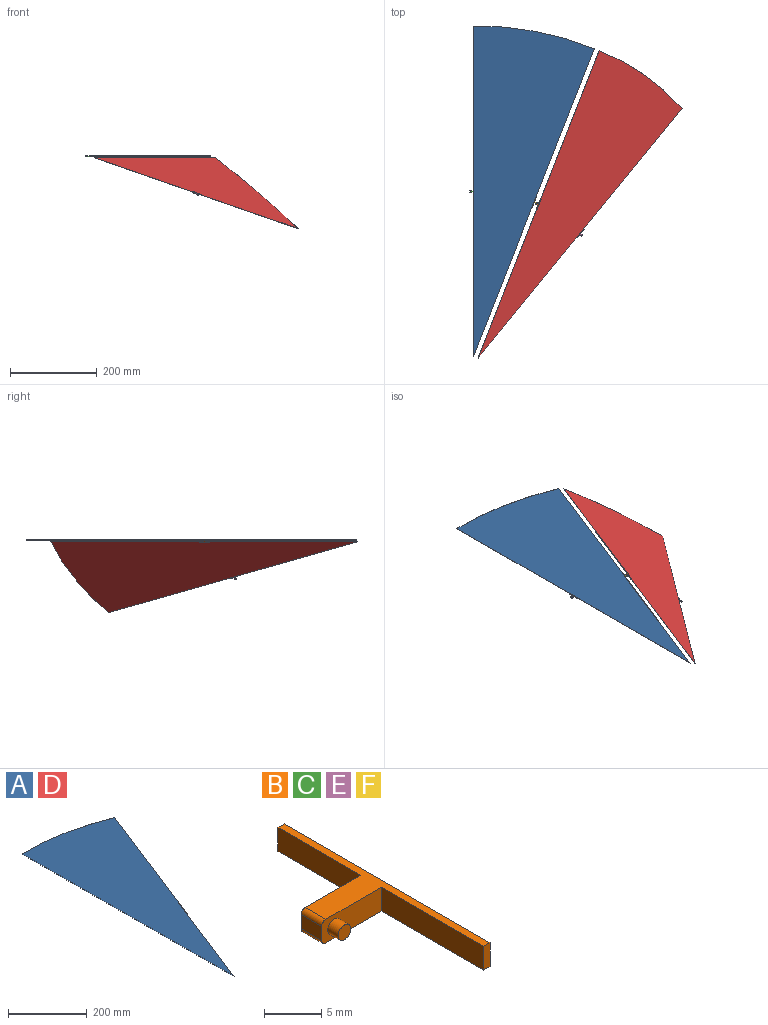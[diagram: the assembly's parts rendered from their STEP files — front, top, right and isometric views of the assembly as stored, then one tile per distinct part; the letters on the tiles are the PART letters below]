
ASSEMBLY  parts=6 mates=5
PART A: 5 faces, bbox 279.3x762.1x0.5 mm
  f0: plane 708.98x279.27mm, normal (0.93,-0.37,0), area 387.1mm2, adj f1,f2,f3,f4
  f1: cylinder r=704.76mm len=279.27mm, axis (0,0,-1), area 145.4mm2, adj f0,f2,f3,f4
  f2: plane 762x0.51mm, normal (-1,0,0), area 387.1mm2, adj f0,f1,f3,f4
  f3: plane 762.08x279.27mm, normal (0,0,1), area 109153.3mm2, adj f0,f1,f2
  f4: plane 762.08x279.27mm, normal (0,0,-1), area 109153.3mm2, adj f0,f1,f2
PART B: 16 faces, bbox 8.1x25.4x2.5 mm
  f0: plane 7.37x2.54mm, normal (0,-1,0), area 16.7mm2, adj f2,f3,f4,f6,f7,f11,f12
  f1: plane 7.37x2.54mm, normal (0,1,0), area 16.7mm2, adj f2,f3,f4,f6,f7,f9,f14
  f2: plane 2.54x1.52mm, normal (-1,0,0), area 3.9mm2, adj f0,f1,f3,f7
  f3: cylinder r=0.51mm len=2.54mm, axis (0,1,0), area 2mm2, adj f0,f1,f2,f4
  f4: plane 25.39x7.62mm, normal (0,0,-1), area 36.8mm2, adj f0,f1,f3,f5,f8,f9,f10,f11
  f5: plane 25.39x2.54mm, normal (1,0,0), area 64.5mm2, adj f4,f6,f8,f10
  f6: plane 25.39x7.62mm, normal (0,0,1), area 36.8mm2, adj f0,f1,f5,f7,f8,f9,f10,f11
  f7: cylinder r=0.51mm len=2.54mm, axis (0,1,0), area 2mm2, adj f0,f1,f2,f6
  f8: plane 2.54x0.76mm, normal (0,1,0), area 1.9mm2, adj f4,f5,f6,f9
  f9: plane 10.22x2.54mm, normal (-1,0,0), area 26mm2, adj f1,f4,f6,f8
  f10: plane 2.54x0.76mm, normal (0,-1,0), area 1.9mm2, adj f4,f5,f6,f11
  f11: plane 12.63x2.54mm, normal (-1,0,0), area 32.1mm2, adj f0,f4,f6,f10
  f12: cylinder r=0.79mm len=1.57mm, axis (0,1,0), area 6.3mm2, adj f0,f13
  f13: plane 1.57x1.57mm, normal (0,-1,0), area 1.9mm2, adj f12
  f14: cylinder r=0.79mm len=1.57mm, axis (0,-1,0), area 6.3mm2, adj f1,f15
  f15: plane 1.57x1.57mm, normal (0,1,0), area 1.9mm2, adj f14
PART C: same geometry as B
PART D: same geometry as A
PART E: same geometry as B
PART F: same geometry as B
PLACE A t=(55.36,4.32,-86.81)mm fixed
PLACE B rot(axis=(-0.94,0.18,0.3),173.4deg) t=(200.19,355.33,-84.64)mm
PLACE C rot(axis=(1,0,0),180deg) t=(47.23,384.11,-85.29)mm
PLACE D rot(axis=(0.16,0.85,-0.5),41.6deg) t=(66.29,-0.13,-90.63)mm
PLACE E rot(axis=(0.33,0,0.94),139.2deg) t=(304.83,282.5,-177.41)mm
PLACE F rot(axis=(-0.19,-0.98,0),180deg) t=(203,356.95,-85.29)mm
MATE revolute B.f12 <-> F.f12  axis (0.37,0.93,0) through (201.58,357.51,-86.56)mm
MATE fastened D.f2 <-> B.f5  axis (-0.75,0.3,0.59) through (206.07,354.3,-90.43)mm
MATE fastened F.f5 <-> A.f0  axis (-0.93,0.37,0) through (195,358.81,-86.56)mm
MATE fastened A.f2 <-> C.f5  axis (-1,0,0) through (55.36,385.32,-86.56)mm
MATE fastened E.f5 <-> D.f0  axis (-0.57,0.62,0.54) through (301.66,288.16,-172.21)mm
